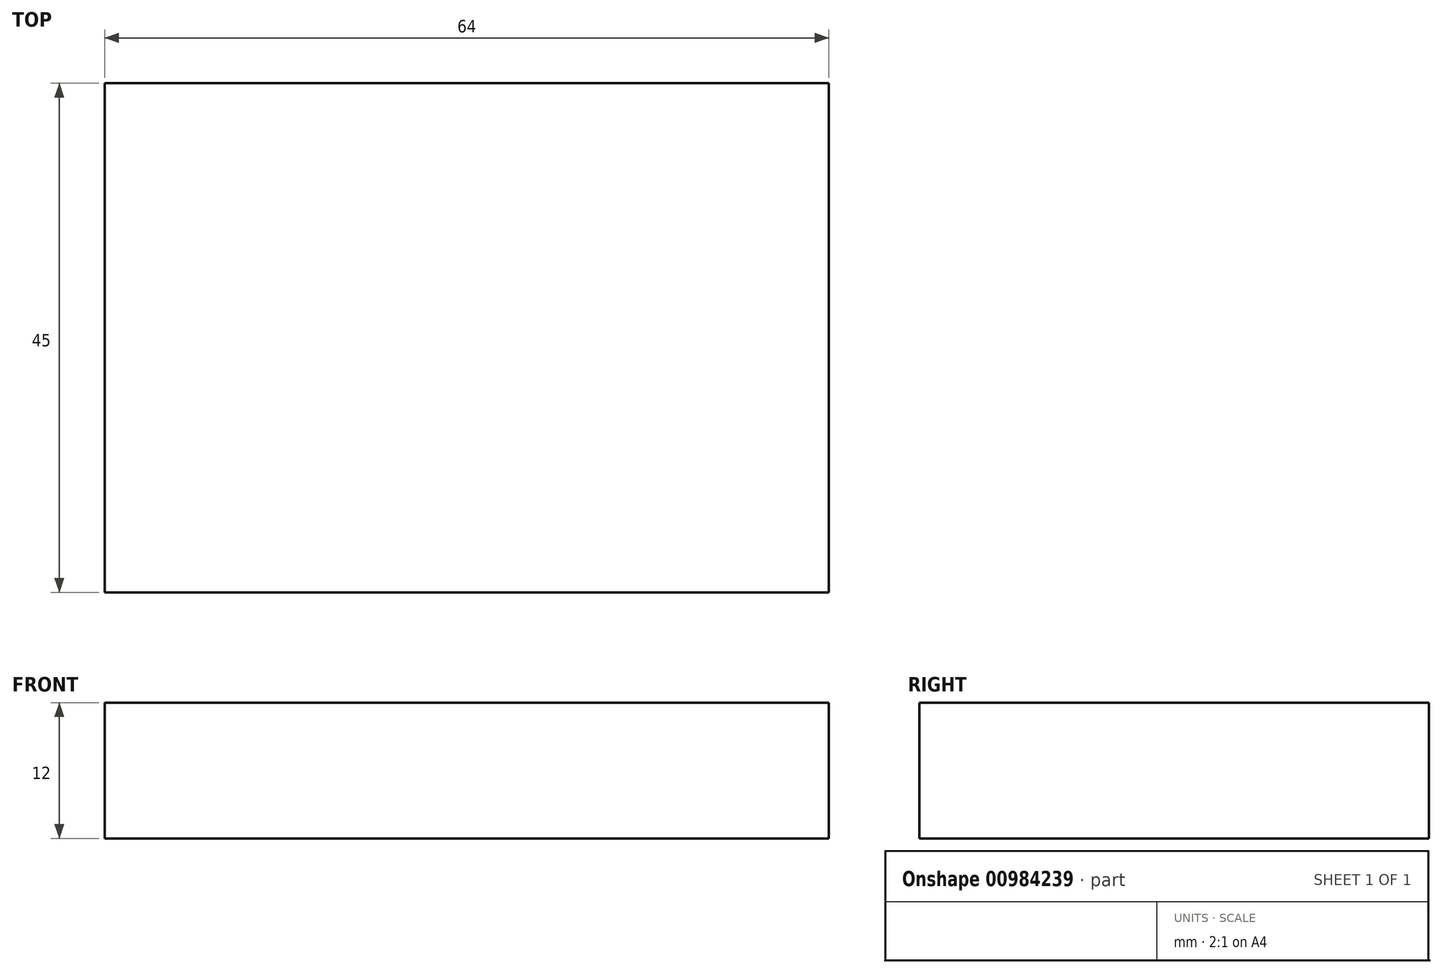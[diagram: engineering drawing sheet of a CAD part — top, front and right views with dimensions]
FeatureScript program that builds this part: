
annotation { "Feature Type Name" : "Feature", "Feature Type Description" : "" }
export const myFeature = defineFeature(function(context is Context, id is Id, definition is map)
    precondition{}
    {
        {
            var Q0;
            Q0=qCreatedBy(makeId("Top.planeOp"),FACE);
            var sketch = newSketch(context, id + "F0", { "sketchPlane" : qUnion([Q0])});
            skLineSegment(sketch, "E0.bottom", {"start": v(32, 22.5) * mm, "end": v(-32, 22.5) * mm});
            skLineSegment(sketch, "E0.top", {"start": v(32, -22.5) * mm, "end": v(-32, -22.5) * mm});
            skLineSegment(sketch, "E0.left", {"start": v(32, 22.5) * mm, "end": v(32, -22.5) * mm});
            skLineSegment(sketch, "E0.right", {"start": v(-32, 22.5) * mm, "end": v(-32, -22.5) * mm});
            skPoint(sketch, "E0.middle", {"position": v(0, 0) * mm});
            skSolve(sketch);
        }
        {
            var Q0;
            Q0=makeQuery(id+"F0.imprint","IMPRINT",FACE,{"disambiguationData":[TD([[makeQuery(id+"F0.imprint","IMPRINT",EDGE,{"derivedFrom":sQuery(id+"F0.wireOp",EDGE,"E0.bottom")}),1.0]])]});
            extrude(context, id + "F1", {"entities" : qUnion([Q0]), "oppositeDirection" : true, "depth" : 12 * mm, "offsetDistance" : 25 * mm});
        }
    });
